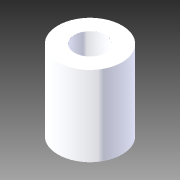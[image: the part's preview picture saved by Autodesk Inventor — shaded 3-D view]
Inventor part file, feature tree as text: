
AUTODESK INVENTOR PART (.ipt)
format: ipt  version: 2012 (Build 160160000, 160)  size: 87,552 bytes
history: native  units: in
note: dims shown in document units (in); Inventor stores cm internally (conversion verified against a paired STEP export)
features: other x1, imported_body x1, extrude x1, sketch x1
ambient origin geometry x8: Origin, YZ Plane, XZ Plane, XY Plane, X Axis, Y Axis, Z Axis, Center Point
feature tree (4):
  parser-record x1  (decoder bookkeeping rows leaked as tree rows — omitted from the tree; the rows remain in map.json)
  imported_body  "Base1"
  extrude  "Extrusion1"  Depth=1.0in TaperAngle=0.0deg
  sketch  "Sketch1"  dims[d0=0.4in d1=1.0in d2=0.0in]
